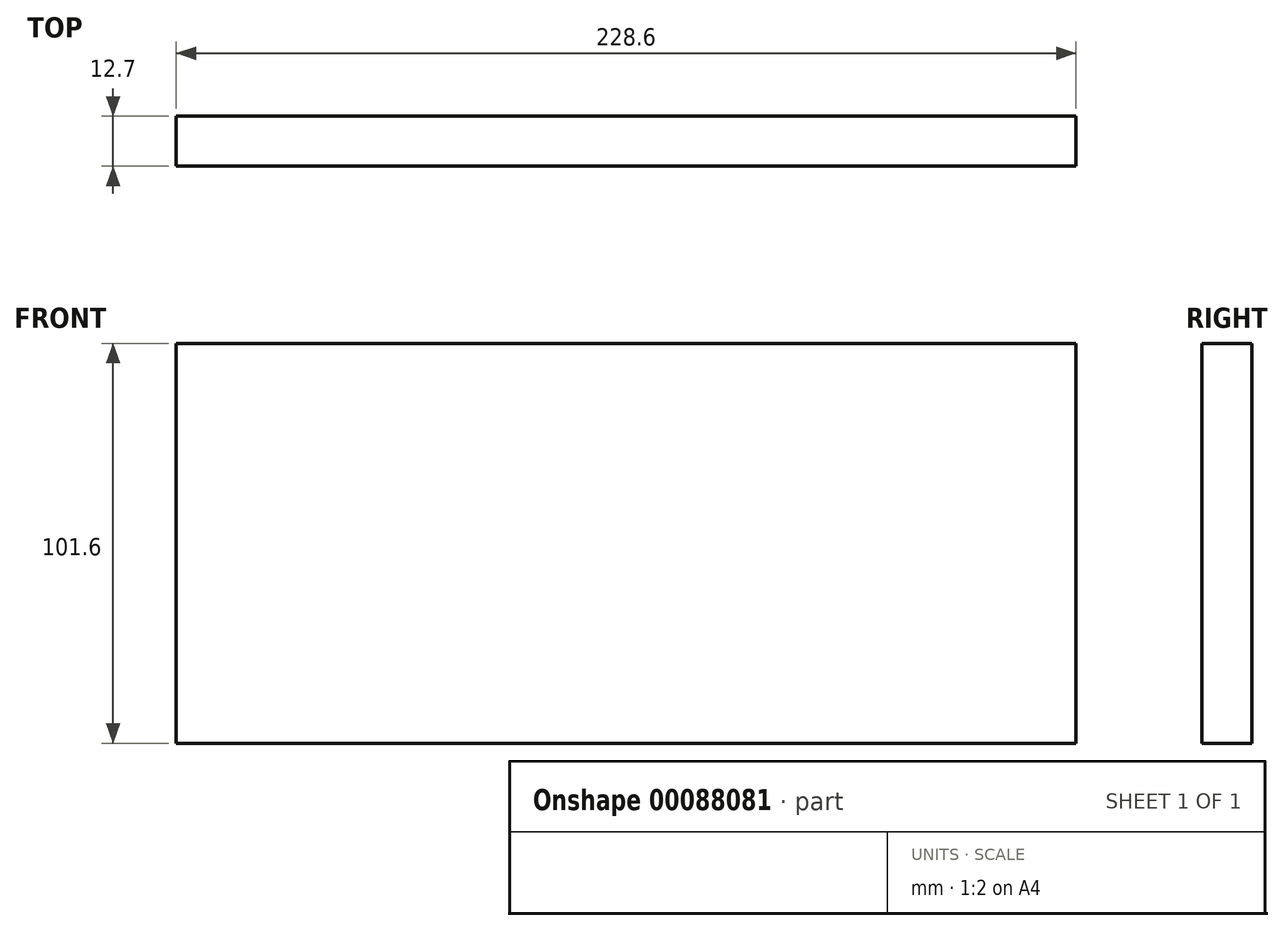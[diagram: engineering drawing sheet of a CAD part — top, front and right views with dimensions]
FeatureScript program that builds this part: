
annotation { "Feature Type Name" : "Feature", "Feature Type Description" : "" }
export const myFeature = defineFeature(function(context is Context, id is Id, definition is map)
    precondition{}
    {
        {
            var Q0;
            Q0=qCreatedBy(makeId("Top.planeOp"),FACE);
            var sketch = newSketch(context, id + "F0", { "sketchPlane" : qUnion([Q0])});
            skLineSegment(sketch, "E0.bottom", {"start": v(-181.82, -6.74) * mm, "end": v(46.78, -6.74) * mm});
            skLineSegment(sketch, "E0.top", {"start": v(-181.82, -19.44) * mm, "end": v(46.78, -19.44) * mm});
            skLineSegment(sketch, "E0.left", {"start": v(-181.82, -6.74) * mm, "end": v(-181.82, -19.44) * mm});
            skLineSegment(sketch, "E0.right", {"start": v(46.78, -6.74) * mm, "end": v(46.78, -19.44) * mm});
            skSolve(sketch);
        }
        {
            var Q0;
            Q0=makeQuery(id+"F0.imprint","IMPRINT",FACE,{"disambiguationData":[TD([[makeQuery(id+"F0.imprint","IMPRINT",EDGE,{"derivedFrom":sQuery(id+"F0.wireOp",EDGE,"E0.bottom")}),-1.0]])]});
            extrude(context, id + "F1", {"entities" : qUnion([Q0]), "depth" : 101.6 * mm});
        }
    });
